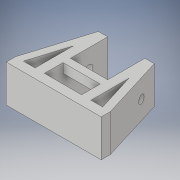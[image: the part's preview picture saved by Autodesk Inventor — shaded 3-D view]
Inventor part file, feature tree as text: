
AUTODESK INVENTOR PART (.ipt)
format: ipt  version: 2018 (Build 220112000, 112)  size: 145,408 bytes
history: native  units: in
note: dims shown in document units (in); Inventor stores cm internally (conversion verified against a paired STEP export)
features: extrude x4, sketch x4
ambient origin geometry x8: Origin, YZ Plane, XZ Plane, XY Plane, X Axis, Y Axis, Z Axis, Center Point
bodies: Solid1 (feature_tree)
feature tree (8):
  extrude  "Extrusion1"  Depth=0.7874in
  extrude  "Extrusion2"  Depth=0.7874in
  extrude  "Extrusion3"  Depth=0.1969in
  extrude  "Extrusion4"  Depth=0.1575in
  sketch  "Sketch1"  dims[d0=2.0079in d1=0.7874in]
  sketch  "Sketch2"  dims[d2=0.1969in d3=0.0in d4=0.7874in]
  sketch  "Sketch3"  dims[d5=0.1969in d6=0.1969in]
  sketch  "Sketch4"  dims[d7=1.3386in d8=0.1575in d9=0.1575in d10=0.1969in d11=0.0in d12=0.1654in d13=0.3937in d14=1.5748in d15=0.0in d16=1.5748in d17=0.0in d18=0.7874in d19=0.1575in d20=0.1969in d21=0.0in]
